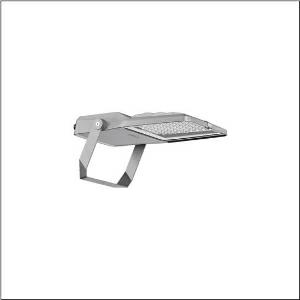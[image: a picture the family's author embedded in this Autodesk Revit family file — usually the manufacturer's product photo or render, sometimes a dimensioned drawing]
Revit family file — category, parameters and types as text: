
# Revit family: floodlight_fl_21_iq_mini___pl33t_5xa7771c4f1a_a815
name_source: partatom
category: Lighting Fixtures
units: mm (PartAtom-declared; Revit-internal decimal feet)

## family parameters
Cut with Voids When Loaded = No
Host = Face
Light Source = No
Part Type = Normal
Room Calculation Point = No
Round Connector Dimension = Use Diameter
Shared = No

## types (1)
- --- (1 x LED, 12570 lm, 87.2 W, 4000K)
    Apparent Load = 87 VA
    CIE Flux Codes = 26 75 99 100 100
    Color Rendering = 70
    Color Temperature = 4000K
    Default Elevation = 1800 mm
    Description = Floodlight FL 21 iQ mini, floodlight, primary light control with lens, of PMMA, primary optical cover: protective disc, of toughened safety glass, transparent, light distribution: PL33T, light emission: direct distribution, installation type: surface-mounted, LED, High Power LED, rated luminous flux: 12.570lm, luminous efficacy: 144lm/W, light colour: 740, colour temperature: 4000K, control gear: iQ Comfort/DALI, control: Auto-Match, Temp-Guard, Lumen-Switch, Night-Set, Smart-Wire, Light-Fading, Desk-Remote (wireless, voltage-free reading and setting of iQ features in the workshop via application-optimized NFC function/RFID function), optimised constant luminous flux control (CLO 2.0), with terminal, 6-pole, mains connection: 220..240V, AC, 50/60Hz, start of lifetime: 87W, end of service life: 92W, reduction: 40W, luminaire housing, of diecast aluminium, powder-coated, Siteco® metallic grey (DB 702S), corrosivity category C5 mid according to DIN EN ISO 12944, suitable for swimming pools, chlorine-resistant, sealing non-destructively replaceable, mounting bracket, of steel, galvanised, powder-coated, Siteco® metallic grey (DB 702S), protection rating (complete): IP66, insulation class (complete): insulation class II (safety insulation), certification: CE, ENEC, VDE, protection symbol: D, impact resistance: IK08, permissible operating ambient temperature: -40..+40°C, permissible operating ambient temperature for outdoor applications: -40..+50°C, standard: DIN EN 12944, LABS conformity tested according to VDMA 24364:2018-05, packaging unit: 1 piece

Light Distribution: PL33T
    Height = 70 mm
    Lamp = 1 x LED
    Lamp Light Flux = 12570 lm
    Lamp Power = 87.2 W
    Lamp count = 1
    Length = 485 mm
    Luminous efficacy = 144 lm/W
    Manufacturer = Siteco
    ModVariant = No
    Model = 5XA7771C4F1A
    Number of Poles = 1
    OnlyDefault = Yes
    Power Factor = 1
    Product Name = Floodlight FL 21 iQ mini | PL33T
    Product group = floodlight | pylon annexe
    ProductGroupID = 6200
    Protection Class = Protection class II
    Protection Degree = IP 66
    RLX_Detail_Level = 1
    RLX_Emergency_Light_Flux = 0 lm
    RLX_Emergency_Type = 0
    RLX_Emergency_Type_DB = No
    RlxData = <blob elided: 96093 chars, md5=e45cce57>
    Socket = socket
    Standby Power = 0 W
    System Light Flux = 12570 lm
    System Power = 87 W
    Type Comments = factory setting: luminous flux: 100 % | dim-lin: 254 | 456 mA
    Type Image = l_1006845.jpg
    URL = http://relux.com
    VarID = @adj_149708
    Voltage = 0 V
    Weight = 0.00 kg
    Width = 337 mm

## geometry (parser evidence)
native form markers: Blend x4, Sweep x13
no freeform markers — native parametric forms only
